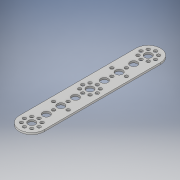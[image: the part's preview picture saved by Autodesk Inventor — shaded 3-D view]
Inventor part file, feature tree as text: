
AUTODESK INVENTOR PART (.ipt)
format: ipt  version: 2019 (Build 230136000, 136)  size: 190,464 bytes
history: native  units: in
note: dims shown in document units (in); Inventor stores cm internally (conversion verified against a paired STEP export)
features: extrude x1, sketch x1
ambient origin geometry x8: Origin, YZ Plane, XZ Plane, XY Plane, X Axis, Y Axis, Z Axis, Center Point
bodies: Solid1 (feature_tree)
feature tree (2):
  extrude  "Extrusion1"  [1 undecoded]
  sketch  "Sketch1"  dims[d0=0.0787in d1=0.0in]
note: 1 required parameter value undecoded (feature->parameter linkage not recoverable at this tier; creation-order binding heuristic only, values carry confidence <= 0.55)
